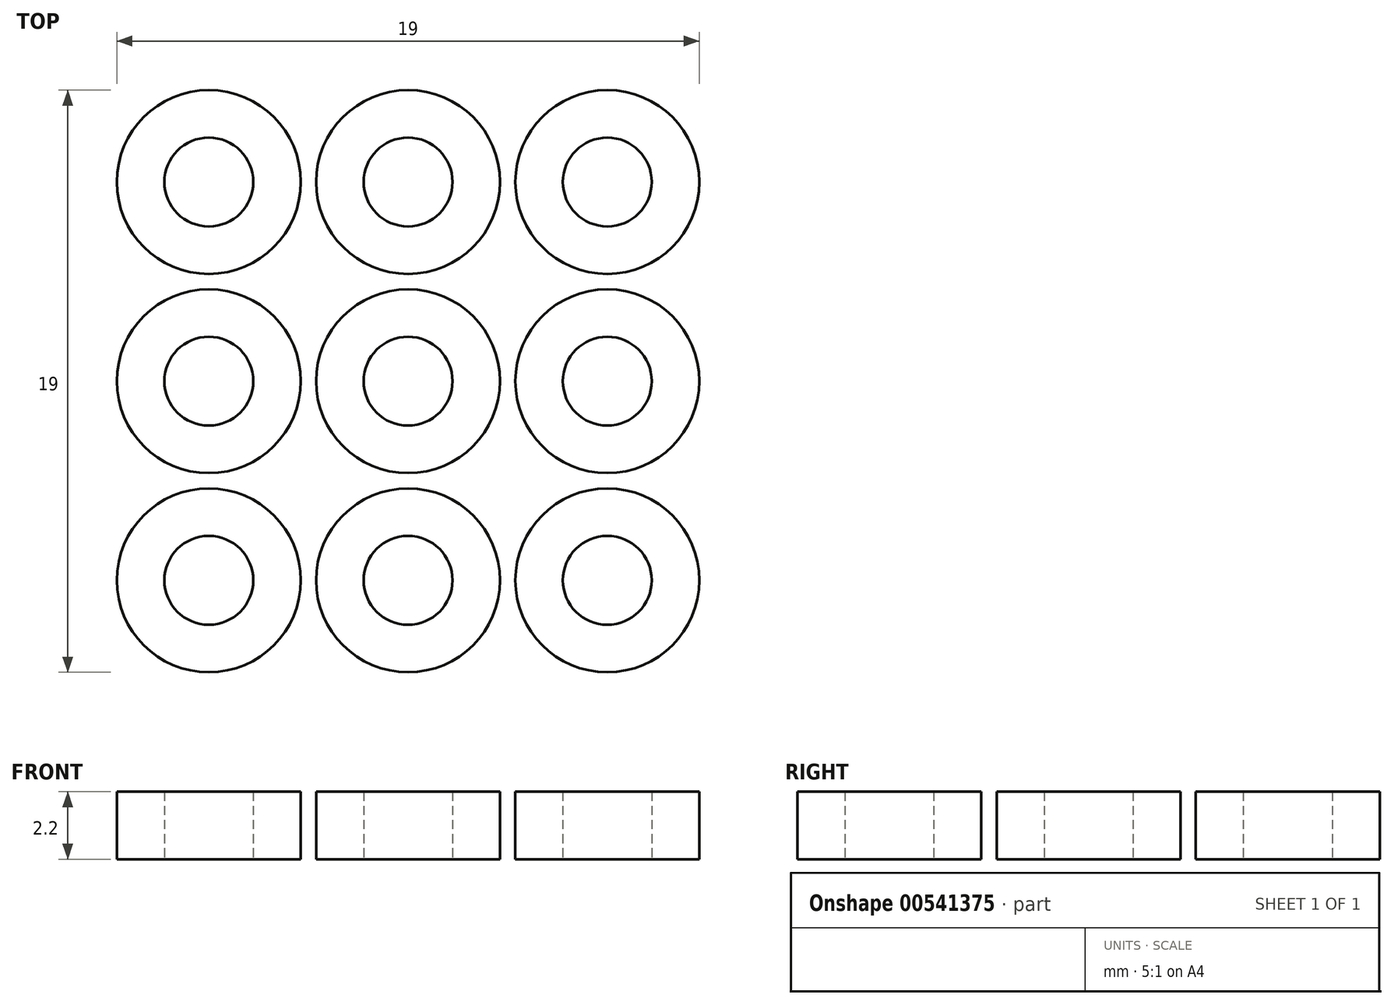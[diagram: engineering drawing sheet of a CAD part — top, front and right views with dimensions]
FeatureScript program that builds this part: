
annotation { "Feature Type Name" : "Feature", "Feature Type Description" : "" }
export const myFeature = defineFeature(function(context is Context, id is Id, definition is map)
    precondition{}
    {
        {
            var Q0;
            Q0=qCreatedBy(makeId("Top.planeOp"),FACE);
            var sketch = newSketch(context, id + "F0", { "sketchPlane" : qUnion([Q0])});
            skCircle(sketch, "E0", {"center": v(0, 0) * mm, "radius": 3 * mm});
            skCircle(sketch, "E1", {"center": v(0, 0) * mm, "radius": 1.45 * mm});
            skCircle(sketch, "E2.0.1.0", {"center": v(0, 6.5) * mm, "radius": 1.45 * mm});
            skCircle(sketch, "E2.0.1.1", {"center": v(0, 6.5) * mm, "radius": 3 * mm});
            skCircle(sketch, "E2.0.2.0", {"center": v(0, 13) * mm, "radius": 1.45 * mm});
            skCircle(sketch, "E2.0.2.1", {"center": v(0, 13) * mm, "radius": 3 * mm});
            skCircle(sketch, "E2.1.0.0", {"center": v(6.5, 0) * mm, "radius": 1.45 * mm});
            skCircle(sketch, "E2.1.0.1", {"center": v(6.5, 0) * mm, "radius": 3 * mm});
            skCircle(sketch, "E2.1.1.0", {"center": v(6.5, 6.5) * mm, "radius": 1.45 * mm});
            skCircle(sketch, "E2.1.1.1", {"center": v(6.5, 6.5) * mm, "radius": 3 * mm});
            skCircle(sketch, "E2.1.2.0", {"center": v(6.5, 13) * mm, "radius": 1.45 * mm});
            skCircle(sketch, "E2.1.2.1", {"center": v(6.5, 13) * mm, "radius": 3 * mm});
            skCircle(sketch, "E2.2.0.0", {"center": v(13, 0) * mm, "radius": 1.45 * mm});
            skCircle(sketch, "E2.2.0.1", {"center": v(13, 0) * mm, "radius": 3 * mm});
            skCircle(sketch, "E2.2.1.0", {"center": v(13, 6.5) * mm, "radius": 1.45 * mm});
            skCircle(sketch, "E2.2.1.1", {"center": v(13, 6.5) * mm, "radius": 3 * mm});
            skCircle(sketch, "E2.2.2.0", {"center": v(13, 13) * mm, "radius": 1.45 * mm});
            skCircle(sketch, "E2.2.2.1", {"center": v(13, 13) * mm, "radius": 3 * mm});
            skLineSegment(sketch, "E2.direction1", {"start": v(0, 0) * mm, "end": v(6.5, 0) * mm, "construction": true});
            skLineSegment(sketch, "E2.direction2", {"start": v(0, 0) * mm, "end": v(0, 6.5) * mm, "construction": true});
            skSolve(sketch);
        }
        {
            var Q0;
            Q0=makeQuery(id+"F0.imprint","IMPRINT",FACE,{"disambiguationData":[TD([[makeQuery(id+"F0.imprint","IMPRINT",EDGE,{"derivedFrom":sQuery(id+"F0.wireOp",EDGE,"E2.2.2.0")}),-1.0]])]});
            var Q1;
            Q1=makeQuery(id+"F0.imprint","IMPRINT",FACE,{"disambiguationData":[TD([[makeQuery(id+"F0.imprint","IMPRINT",EDGE,{"derivedFrom":sQuery(id+"F0.wireOp",EDGE,"E2.1.2.0")}),-1.0]])]});
            var Q2;
            Q2=makeQuery(id+"F0.imprint","IMPRINT",FACE,{"disambiguationData":[TD([[makeQuery(id+"F0.imprint","IMPRINT",EDGE,{"derivedFrom":sQuery(id+"F0.wireOp",EDGE,"E2.0.2.0")}),-1.0]])]});
            var Q3;
            Q3=makeQuery(id+"F0.imprint","IMPRINT",FACE,{"disambiguationData":[TD([[makeQuery(id+"F0.imprint","IMPRINT",EDGE,{"derivedFrom":sQuery(id+"F0.wireOp",EDGE,"E2.0.1.0")}),-1.0]])]});
            var Q4;
            Q4=makeQuery(id+"F0.imprint","IMPRINT",FACE,{"disambiguationData":[TD([[makeQuery(id+"F0.imprint","IMPRINT",EDGE,{"derivedFrom":sQuery(id+"F0.wireOp",EDGE,"E2.1.1.0")}),-1.0]])]});
            var Q5;
            Q5=makeQuery(id+"F0.imprint","IMPRINT",FACE,{"disambiguationData":[TD([[makeQuery(id+"F0.imprint","IMPRINT",EDGE,{"derivedFrom":sQuery(id+"F0.wireOp",EDGE,"E2.2.1.0")}),-1.0]])]});
            var Q6;
            Q6=makeQuery(id+"F0.imprint","IMPRINT",FACE,{"disambiguationData":[TD([[makeQuery(id+"F0.imprint","IMPRINT",EDGE,{"derivedFrom":sQuery(id+"F0.wireOp",EDGE,"E2.2.0.0")}),-1.0]])]});
            var Q7;
            Q7=makeQuery(id+"F0.imprint","IMPRINT",FACE,{"disambiguationData":[TD([[makeQuery(id+"F0.imprint","IMPRINT",EDGE,{"derivedFrom":sQuery(id+"F0.wireOp",EDGE,"E2.1.0.0")}),-1.0]])]});
            var Q8;
            Q8=makeQuery(id+"F0.imprint","IMPRINT",FACE,{"disambiguationData":[TD([[makeQuery(id+"F0.imprint","IMPRINT",EDGE,{"derivedFrom":sQuery(id+"F0.wireOp",EDGE,"E0")}),1.0]])]});
            extrude(context, id + "F1", {"entities" : qUnion([Q0, Q1, Q2, Q3, Q4, Q5, Q6, Q7, Q8]), "depth" : 2.2 * mm, "offsetDistance" : 25 * mm});
        }
    });
